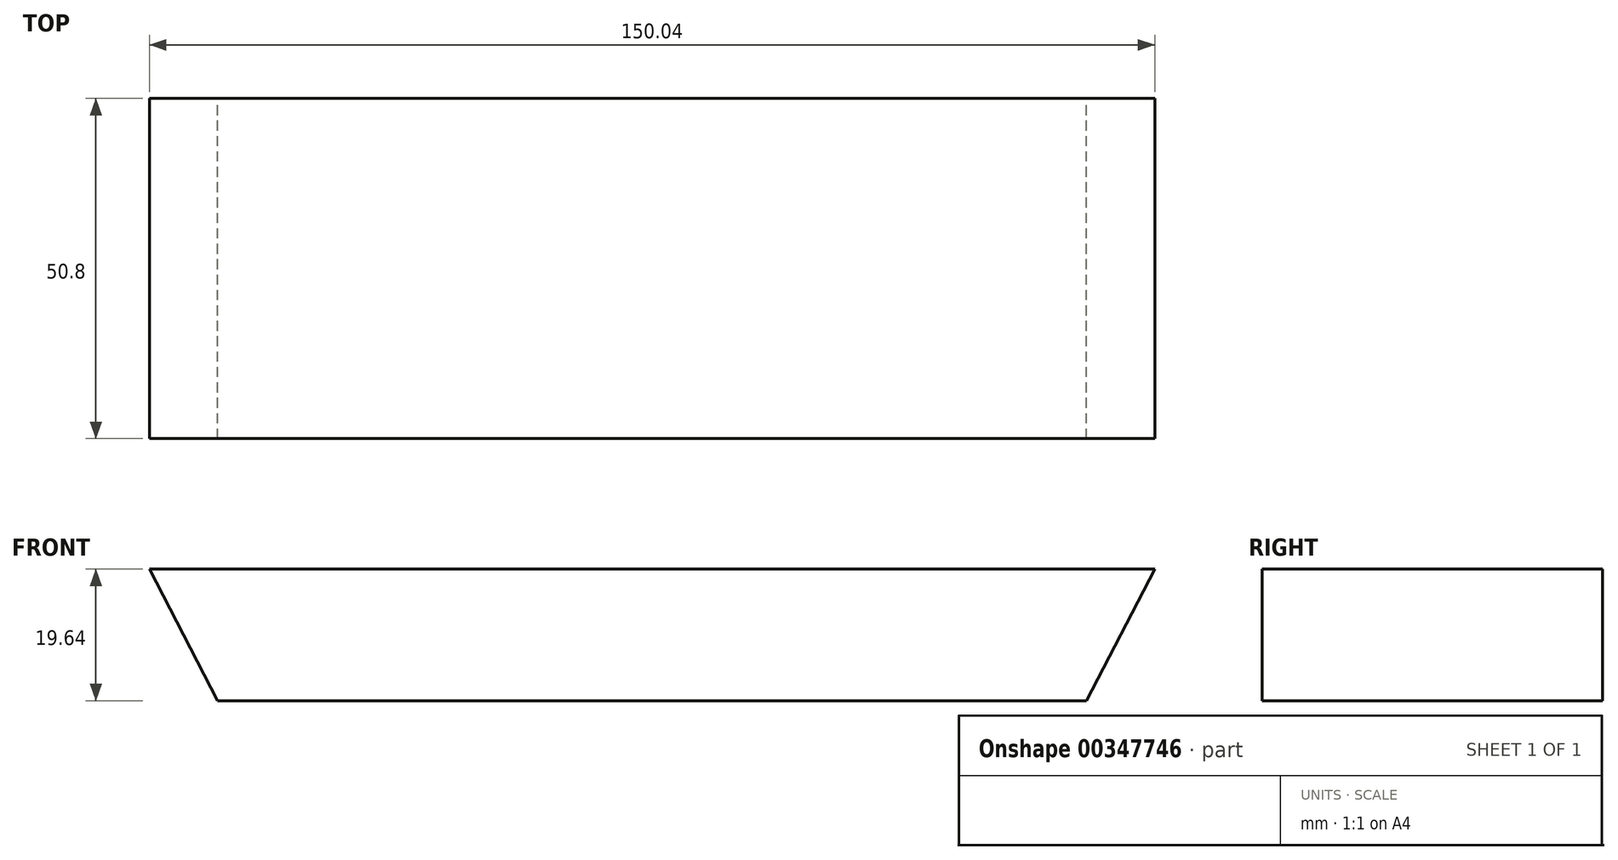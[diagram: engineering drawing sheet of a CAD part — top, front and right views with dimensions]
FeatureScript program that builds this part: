
annotation { "Feature Type Name" : "Feature", "Feature Type Description" : "" }
export const myFeature = defineFeature(function(context is Context, id is Id, definition is map)
    precondition{}
    {
        {
            var Q0;
            Q0=qCreatedBy(makeId("Front.planeOp"),FACE);
            var sketch = newSketch(context, id + "F0", { "sketchPlane" : qUnion([Q0])});
            skLineSegment(sketch, "E0", {"start": v(75.02, 19.64) * mm, "end": v(64.84, 0) * mm});
            skLineSegment(sketch, "E1.MirrorCS", {"start": v(-75.02, 19.64) * mm, "end": v(-64.84, 0) * mm});
            skLineSegment(sketch, "E2", {"start": v(-75.02, 19.64) * mm, "end": v(75.02, 19.64) * mm});
            skLineSegment(sketch, "E3", {"start": v(64.84, 0) * mm, "end": v(-64.84, 0) * mm});
            skSolve(sketch);
        }
        {
            var Q0;
            Q0=makeQuery(id+"F0.imprint","IMPRINT",FACE,{"disambiguationData":[TD([[makeQuery(id+"F0.imprint","IMPRINT",EDGE,{"derivedFrom":sQuery(id+"F0.wireOp",EDGE,"E0")}),-1.0]])]});
            extrude(context, id + "F1", {"entities" : qUnion([Q0]), "depth" : 50.8 * mm});
        }
    });
